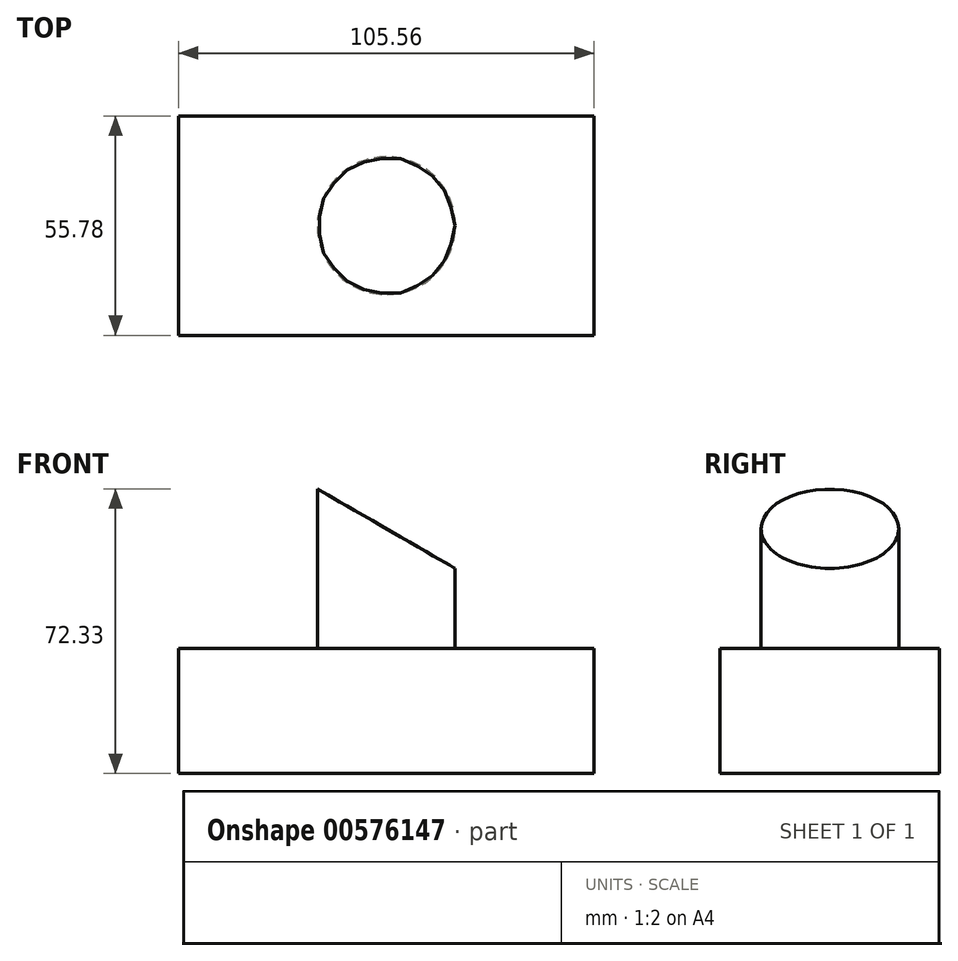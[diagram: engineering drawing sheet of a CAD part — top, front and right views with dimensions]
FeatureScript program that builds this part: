
annotation { "Feature Type Name" : "Feature", "Feature Type Description" : "" }
export const myFeature = defineFeature(function(context is Context, id is Id, definition is map)
    precondition{}
    {
        {
            var Q0;
            Q0=qCreatedBy(makeId("Top.planeOp"),FACE);
            var sketch = newSketch(context, id + "F0", { "sketchPlane" : qUnion([Q0])});
            skLineSegment(sketch, "E0.bottom", {"start": v(-52.78, 27.9) * mm, "end": v(52.78, 27.9) * mm});
            skLineSegment(sketch, "E0.top", {"start": v(-52.78, -27.9) * mm, "end": v(52.78, -27.9) * mm});
            skLineSegment(sketch, "E0.left", {"start": v(-52.78, 27.9) * mm, "end": v(-52.78, -27.9) * mm});
            skLineSegment(sketch, "E0.right", {"start": v(52.78, 27.9) * mm, "end": v(52.78, -27.9) * mm});
            skPoint(sketch, "E0.middle", {"position": v(0, 0) * mm});
            skSolve(sketch);
        }
        {
            var Q0;
            Q0=makeQuery(id+"F0.imprint","IMPRINT",FACE,{"disambiguationData":[TD([[makeQuery(id+"F0.imprint","IMPRINT",EDGE,{"derivedFrom":sQuery(id+"F0.wireOp",EDGE,"E0.bottom")}),-1.0]])]});
            extrude(context, id + "F1", {"entities" : qUnion([Q0]), "depth" : 31.75 * mm, "offsetDistance" : 25.4 * mm});
        }
        {
            var Q0;
            Q0=makeQuery(id+"F1.opExtrude","CAP_EDGE",EDGE,{"disambiguationData":[OSD([sQuery(id+"F0.wireOp",EDGE,"E0.right")])],"isStart":false});
            cPlane(context, id + "F2", {"entities" : qUnion([Q0]), "cplaneType" : CPlaneType.LINE_ANGLE, "offset" : 25.4 * mm, "angle" : 30 * degree, "oppositeDirection" : true, "width" : 152.4 * mm, "height" : 152.4 * mm});
        }
        {
            var Q0;
            Q0=makeQuery(id+"F1.opExtrude","CAP_FACE",FACE,{"disambiguationData":[OSD([sQuery(id+"F0.wireOp",EDGE,"E0.bottom"),sQuery(id+"F0.wireOp",EDGE,"E0.top"),sQuery(id+"F0.wireOp",EDGE,"E0.left"),sQuery(id+"F0.wireOp",EDGE,"E0.right")])],"isStart":false});
            var sketch = newSketch(context, id + "F3", { "sketchPlane" : qUnion([Q0])});
            skCircle(sketch, "E1", {"center": v(0, 0) * mm, "radius": 17.5 * mm});
            skSolve(sketch);
        }
        {
            var Q0;
            Q0=makeQuery(id+"F3.imprint","IMPRINT",FACE,{"disambiguationData":[TD([[makeQuery(id+"F3.imprint","IMPRINT",EDGE,{"derivedFrom":sQuery(id+"F3.wireOp",EDGE,"E1")}),1.0]])]});
            var Q1;
            Q1=qCreatedBy(id+"F2.planeOp",FACE);
            extrude(context, id + "F4", {"entities" : qUnion([Q0]), "operationType" : NewBodyOperationType.ADD, "endBound" : BoundingType.UP_TO_SURFACE, "depth" : 31.75 * mm, "endBoundEntityFace" : qUnion([Q1]), "offsetDistance" : 25.4 * mm});
        }
    });
